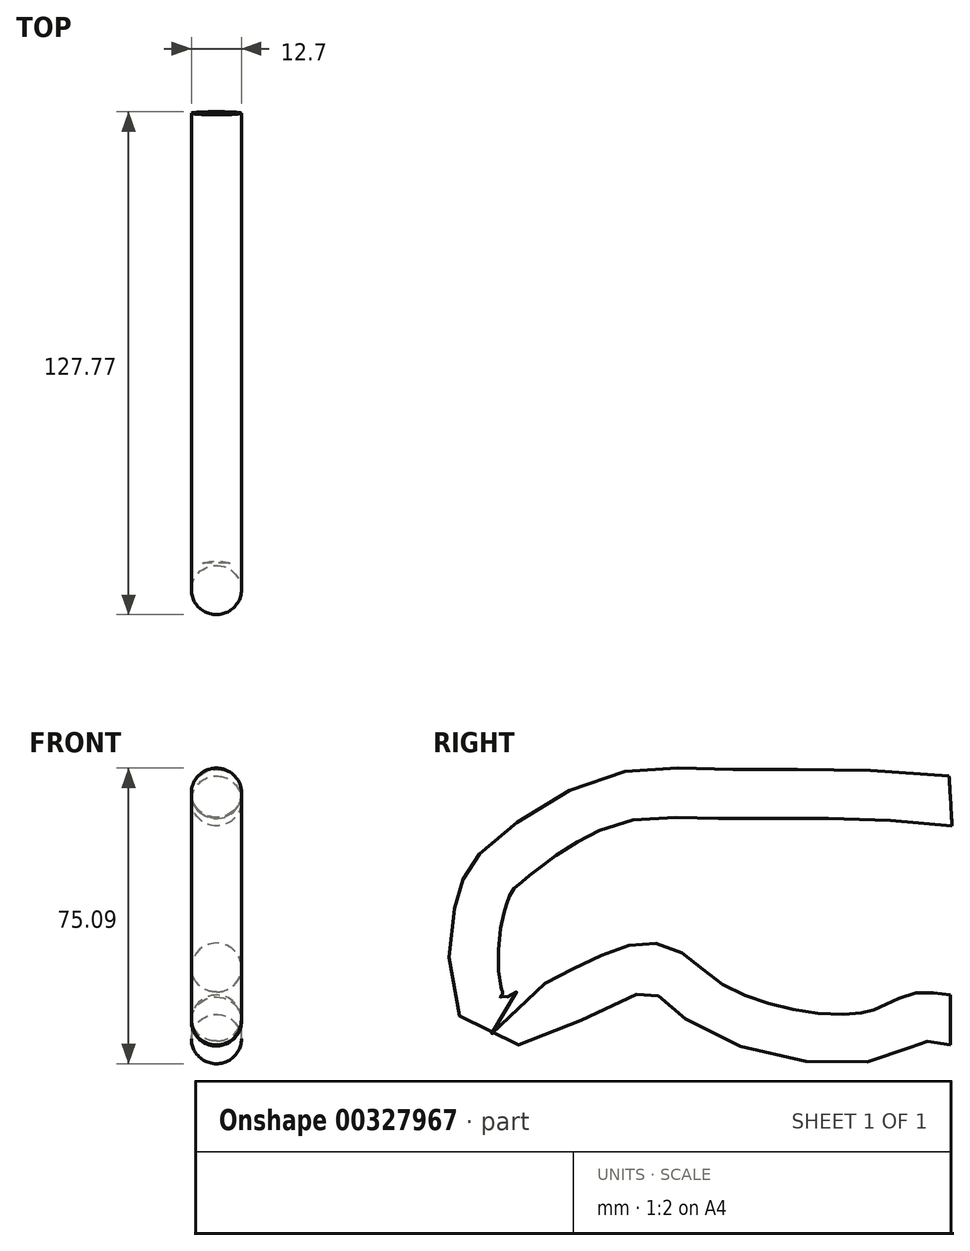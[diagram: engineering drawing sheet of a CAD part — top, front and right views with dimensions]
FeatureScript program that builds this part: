
annotation { "Feature Type Name" : "Feature", "Feature Type Description" : "" }
export const myFeature = defineFeature(function(context is Context, id is Id, definition is map)
    precondition{}
    {
        {
            var Q0;
            Q0=qCreatedBy(makeId("Right.planeOp"),FACE);
            var sketch = newSketch(context, id + "F0", { "sketchPlane" : qUnion([Q0])});
            skFitSpline(sketch, "E0", {"points": [v(0, 0) * mm, v(-10.1, 0) * mm, v(-22.5, -4.48) * mm, v(-61.3, 3.79) * mm, v(-78.29, 13.2) * mm, v(-115.02, 0) * mm, v(-120.76, 21.93) * mm, v(-117.78, 34.1) * mm, v(-115.48, 37.54) * mm, v(-90.23, 54.53) * mm, v(-59.46, 57.51) * mm, v(0, 55.67) * mm], "startDerivative": vector(-277.87, 48.84) * mm, "endDerivative": vector(458.59, -53.1) * mm});
            skSolve(sketch);
        }
        {
            var Q0;
            Q0=qCreatedBy(makeId("Front.planeOp"),FACE);
            var sketch = newSketch(context, id + "F1", { "sketchPlane" : qUnion([Q0])});
            skCircle(sketch, "E1", {"center": v(0, 0) * mm, "radius": 6.35 * mm});
            skSolve(sketch);
        }
        {
            var Q0;
            Q0=makeQuery(id+"F1.imprint","IMPRINT",FACE,{"disambiguationData":[TD([[makeQuery(id+"F1.imprint","IMPRINT",EDGE,{"derivedFrom":sQuery(id+"F1.wireOp",EDGE,"E1")}),1.0]])]});
            var Q1;
            Q1=sQuery(id+"F0.wireOp",EDGE,"E0");
            sweep(context, id + "F2", {"profiles" : qUnion([Q0]), "path" : qUnion([Q1])});
        }
    });
